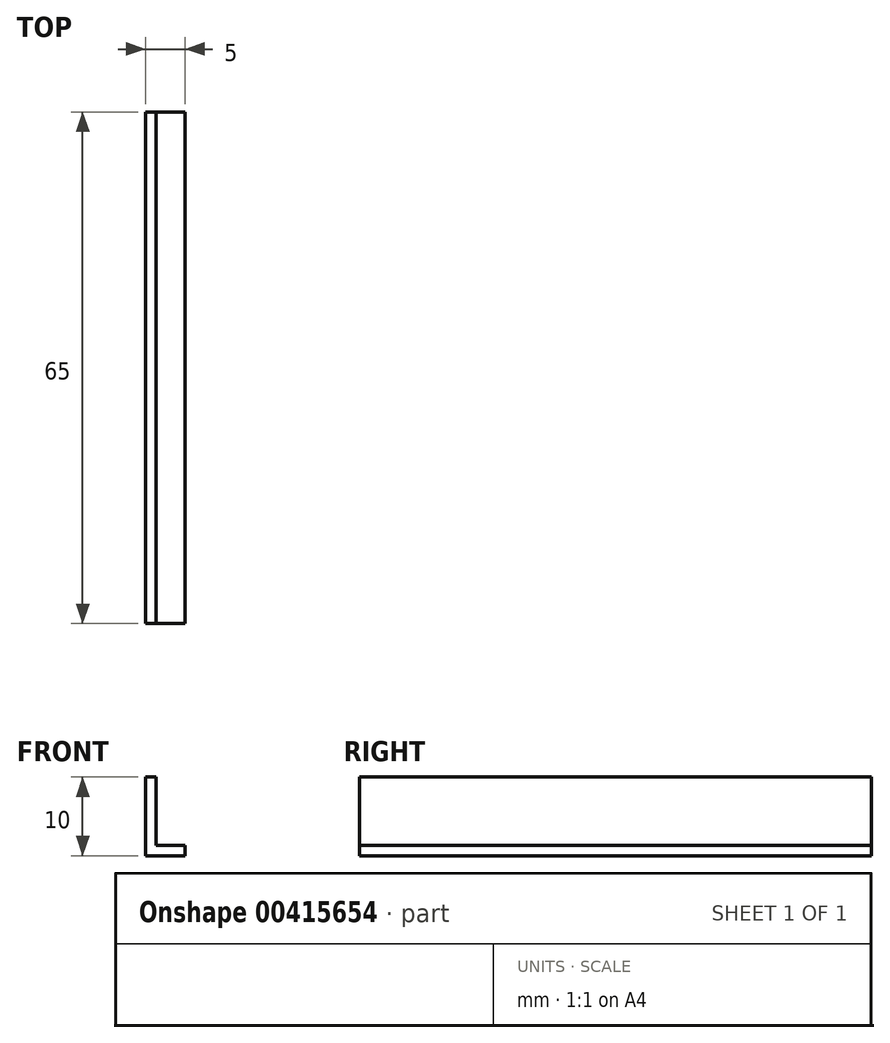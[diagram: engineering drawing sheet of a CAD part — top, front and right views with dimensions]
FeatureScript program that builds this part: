
annotation { "Feature Type Name" : "Feature", "Feature Type Description" : "" }
export const myFeature = defineFeature(function(context is Context, id is Id, definition is map)
    precondition{}
    {
        {
            var Q0;
            Q0=qCreatedBy(makeId("Front.planeOp"),FACE);
            var sketch = newSketch(context, id + "F0", { "sketchPlane" : qUnion([Q0])});
            skLineSegment(sketch, "E0", {"start": v(0, 0) * mm, "end": v(0, 10) * mm});
            skLineSegment(sketch, "E1", {"start": v(0, 10) * mm, "end": v(1.3, 10) * mm});
            skLineSegment(sketch, "E2", {"start": v(1.3, 10) * mm, "end": v(1.3, 1.3) * mm});
            skLineSegment(sketch, "E3", {"start": v(1.3, 1.3) * mm, "end": v(5, 1.3) * mm});
            skLineSegment(sketch, "E4", {"start": v(5, 1.3) * mm, "end": v(5, 0) * mm});
            skLineSegment(sketch, "E5", {"start": v(5, 0) * mm, "end": v(0, 0) * mm});
            skSolve(sketch);
        }
        {
            var Q0;
            Q0 = qSketchRegion(id + "F0", true);
            extrude(context, id + "F1", {"entities" : qUnion([Q0]), "endBound" : BoundingType.SYMMETRIC, "depth" : 65 * mm});
        }
    });
